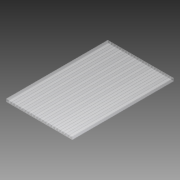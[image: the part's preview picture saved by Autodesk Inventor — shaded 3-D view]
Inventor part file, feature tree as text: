
AUTODESK INVENTOR PART (.ipt)
format: ipt  version: 2012 (Build 160160000, 160)  size: 201,216 bytes
history: native  units: in
note: dims shown in document units (in); Inventor stores cm internally (conversion verified against a paired STEP export)
features: other x3, sketch x1
ambient origin geometry x8: Origin, YZ Plane, XZ Plane, XY Plane, X Axis, Y Axis, Z Axis, Center Point
bodies: Solid1 (feature_tree)
feature tree (4):
  other  "8 ball polycarb side.ipt"
  other  "Solid1::8 ball polycarb side.ipt"
  sketch  "Sketch1"  dims[d0=0.3937in]
  other  "TaggingFeature1"
